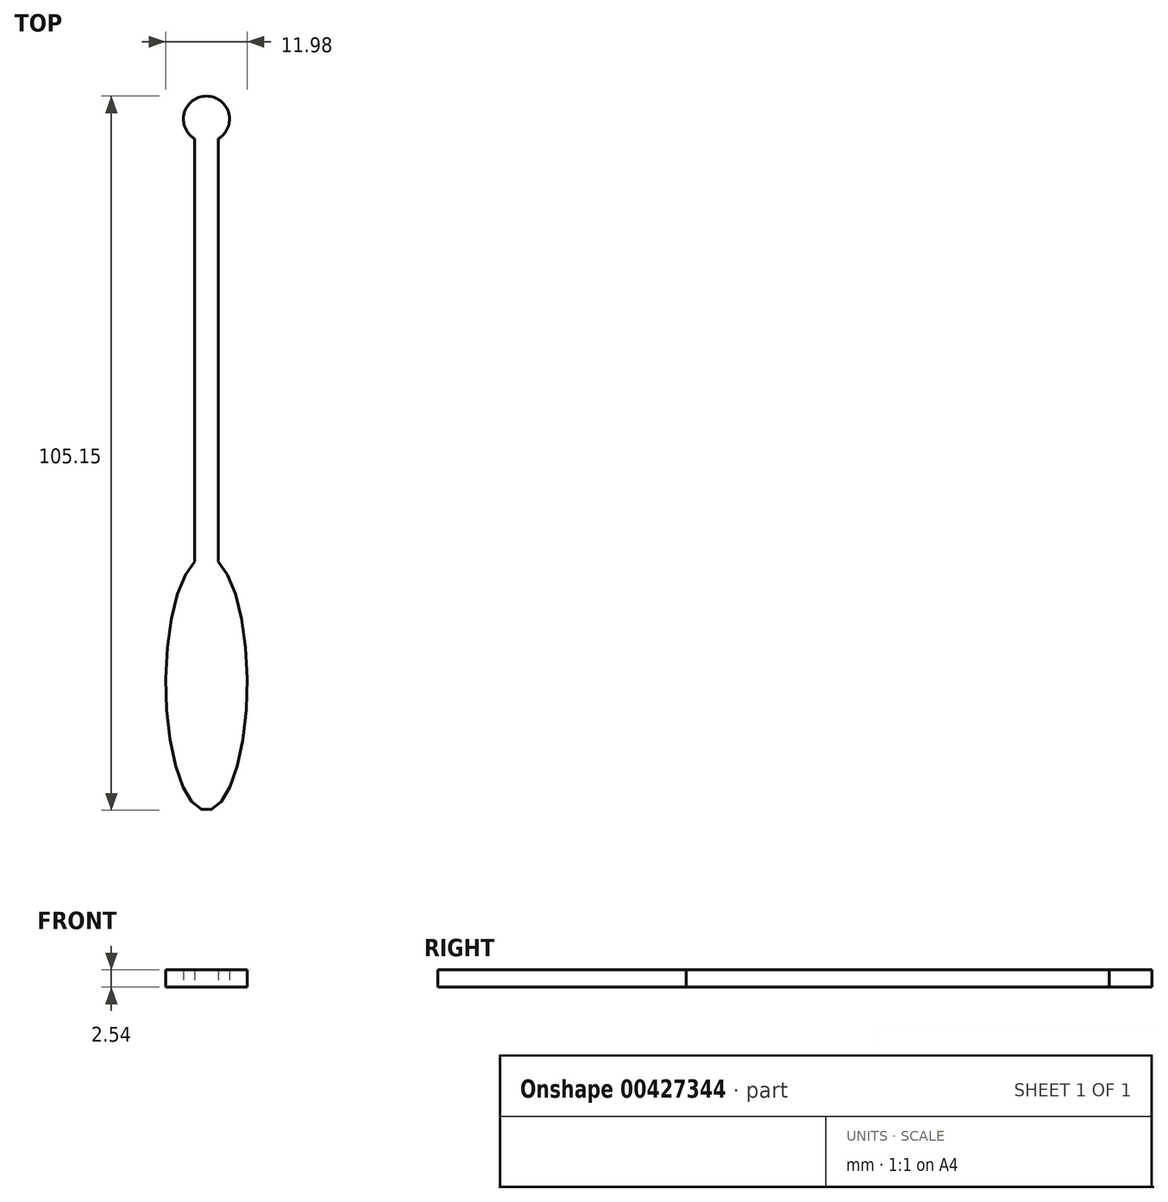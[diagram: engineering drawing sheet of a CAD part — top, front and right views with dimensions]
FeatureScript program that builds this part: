
annotation { "Feature Type Name" : "Feature", "Feature Type Description" : "" }
export const myFeature = defineFeature(function(context is Context, id is Id, definition is map)
    precondition{}
    {
        {
            var Q0;
            Q0=qCreatedBy(makeId("Top.planeOp"),FACE);
            var sketch = newSketch(context, id + "F0", { "sketchPlane" : qUnion([Q0])});
            skLineSegment(sketch, "E0.bottom", {"start": v(-27.75, 45.48) * mm, "end": v(-24.22, 45.48) * mm});
            skLineSegment(sketch, "E0.top", {"start": v(-27.75, -37.57) * mm, "end": v(-24.22, -37.57) * mm});
            skLineSegment(sketch, "E0.left", {"start": v(-27.75, 45.48) * mm, "end": v(-27.75, -37.57) * mm});
            skLineSegment(sketch, "E0.right", {"start": v(-24.22, 45.48) * mm, "end": v(-24.22, -37.57) * mm});
            skCircle(sketch, "E1", {"center": v(-25.98, 45.48) * mm, "radius": 3.39 * mm});
            skEllipse(sketch, "E2", {"center": v(-25.98, -37.57) * mm, "majorRadius": 18.7 * mm, "minorRadius": 5.99 * mm, "majorAxis": v(0, -1)});
            skSolve(sketch);
        }
        {
            var Q0;
            {var subQ0=sQuery(id+"F0.wireOp",EDGE,"E0.top");Q0=makeQuery(id+"F0.imprint","IMPRINT",FACE,{"disambiguationData":[TD([[makeQuery(id+"F0.imprint","IMPRINT",EDGE,{"derivedFrom":subQ0}),1.0]])]});}
            var Q1;
            {var subQ0=sQuery(id+"F0.wireOp",EDGE,"E0.top");Q1=makeQuery(id+"F0.imprint","IMPRINT",FACE,{"disambiguationData":[TD([[makeQuery(id+"F0.imprint","IMPRINT",EDGE,{"derivedFrom":subQ0}),-1.0]])]});}
            var Q2;
            {var subQ0=sQuery(id+"F0.wireOp",EDGE,"E1");var subQ1=sQuery(id+"F0.wireOp",EDGE,"E0.left");var subQ2=makeQuery(id+"F0.imprint","INTERSECT",VERTEX,{"derivedFrom":[subQ1,subQ0]});Q2=makeQuery(id+"F0.imprint","IMPRINT",FACE,{"disambiguationData":[TD([[makeQuery(id+"F0.imprint","IMPRINT",EDGE,{"disambiguationData":[TD([[subQ2,-1.0]])],"derivedFrom":subQ1}),1.0]])]});}
            var Q3;
            {var subQ0=sQuery(id+"F0.wireOp",EDGE,"E0.bottom");Q3=makeQuery(id+"F0.imprint","IMPRINT",FACE,{"disambiguationData":[TD([[makeQuery(id+"F0.imprint","IMPRINT",EDGE,{"derivedFrom":subQ0}),1.0]])]});}
            var Q4;
            {var subQ0=sQuery(id+"F0.wireOp",EDGE,"E0.bottom");Q4=makeQuery(id+"F0.imprint","IMPRINT",FACE,{"disambiguationData":[TD([[makeQuery(id+"F0.imprint","IMPRINT",EDGE,{"derivedFrom":subQ0}),-1.0]])]});}
            extrude(context, id + "F1", {"entities" : qUnion([Q0, Q1, Q2, Q3, Q4]), "depth" : 2.54 * mm});
        }
    });
